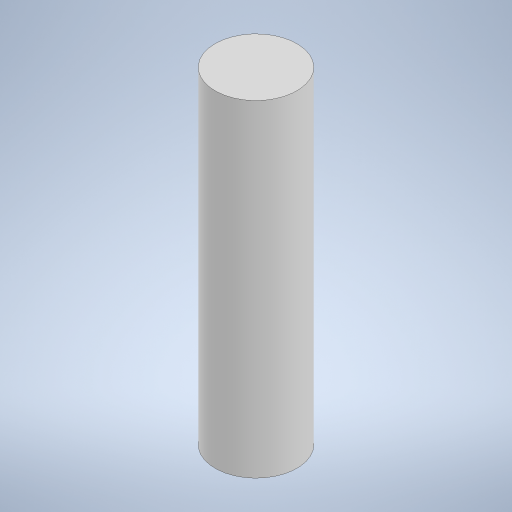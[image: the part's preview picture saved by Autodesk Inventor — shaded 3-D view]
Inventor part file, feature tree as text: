
AUTODESK INVENTOR PART (.ipt)
format: ipt  version: 2024.2 (Build 282272000, 272)  size: 212,480 bytes
history: native  units: mm
features: extrude x1, sketch x1
ambient origin geometry x8: Origin, YZ Plane, XZ Plane, XY Plane, X Axis, Y Axis, Z Axis, Center Point
bodies: Solid1 (feature_tree)
feature tree (2):
  extrude  "Extrusion1"  Depth=10.0mm TaperAngle=0.0deg
  sketch  "Sketch1"  dims[d0=2.5mm d1=10.0mm d2=0.0mm]
